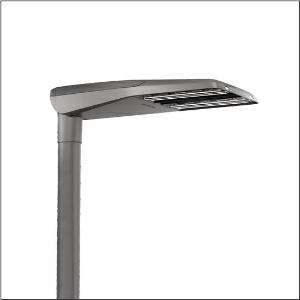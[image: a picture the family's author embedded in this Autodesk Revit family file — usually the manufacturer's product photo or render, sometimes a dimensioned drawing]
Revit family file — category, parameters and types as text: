
# Revit family: streetlight_sl_11_iq_midi___pc-r_5xc3f11f08me_40c1
name_source: partatom
category: Lighting Fixtures
units: mm (PartAtom-declared; Revit-internal decimal feet)

## family parameters
Cut with Voids When Loaded = No
Host = Face
Light Source = No
Part Type = Normal
Room Calculation Point = No
Round Connector Dimension = Use Diameter
Shared = No

## types (1)
- --- (1 x LED, 9590 lm, 124.5 W, 1800K)
    Apparent Load = 125 VA
    CIE Flux Codes = 37 73 96 100 100
    Color Rendering = 70
    Color Temperature = 1800K
    Default Elevation = 1800 mm  [stored 5.90551 ft]
    Description = Streetlight SL 11 iQ midi, mast luminaire, primary light control with 3 zone facetted reflector, of plastic, silver coated, highly specular, primary optical cover: cover, of PMMA, transparent, light distribution: PC-R, light emission: direct distribution, primary light characteristic: asymmetric, right, installation type: post-top, side-entry, LED, High Power LED, rated luminous flux: 9.590lm, luminous efficacy: 77lm/W, light colour: 718, colour temperature: 1800K, control: Street-Remote, Auto-Match, Temp-Guard, Lumen-Switch, Night-Set, Smart-Wire, Light-Fading, Desk-Remote (wireless, voltage-free reading and setting of iQ features in the workshop via application-optimized NFC function/RFID function), optimised constant luminous flux control (CLO 2.0), with cable H07RN-F 5x 1.5mm², mains connection: 230..240V, AC, 50/60Hz, connection cable pre-assembled, cable length: 12,5m, start of lifetime: 125W, end of service life: 132W, reduction: 55W, luminaire housing, of diecast aluminium, powder-coated, Siteco® metallic grey (DB 702S), please order mast flange separately, inclination adjustable without tools: 0°, 5°, 10°, 15° (post-top) | 0°, -5°, -10°, -15° (side-entry), sealing non-destructively replaceable, multi-level sealing system, length: 780mm, width: 376mm, height: 118mm, mast flange for spigot size: 42mm (side-entry): 5XC10008XM4, 60/48mm (side-entry/post-top): 5XC10108XM2, 76/60mm (side-entry/post-top): 5XC10108XM1, equipment: Power, protection rating (complete): IP66, insulation class (complete): insulation class II (safety insulation), certification: CE, ENEC, VDE, impact resistance: IK09, permissible operating ambient temperature for outdoor applications: -25..+50°C, standard-compliant lighting for roads and squares, Environmental Product Declaration (EPD) tested and certified by an independent institute, packaging unit: 1 piece

Light Distribution: PC-R
    Height = 118 mm
    Lamp = 1 x LED
    Lamp Light Flux = 9590 lm
    Lamp Power = 124.5 W
    Lamp count = 1
    Length = 780 mm
    Luminous efficacy = 77 lm/W
    Manufacturer = Siteco
    ModVariant = No
    Model = 5XC3F11F08ME
    Number of Poles = 1
    OnlyDefault = Yes
    Power Factor = 1
    Product Name = Streetlight SL 11 iQ midi | PC-R
    Product group = mast luminaire | pylon top
    ProductGroupID = 6100
    Protection Class = Protection class II
    Protection Degree = IP 66
    RLX_Detail_Level = 1
    RLX_Emergency_Light_Flux = 0 lm
    RLX_Emergency_Type = 0
    RLX_Emergency_Type_DB = No
    RlxData = <blob elided: 74545 chars, md5=f4a8ba47>
    Socket = socket
    Standby Power = 0 W
    System Light Flux = 9590 lm
    System Power = 125 W
    Type Comments = factory setting: luminous flux: 100 % | dim-lin: 254 | 554 mA
    Type Image = l_1005960.jpg
    URL = http://relux.com
    VarID = @adj_009967
    Voltage = 0 V
    Weight = 0.00 kg
    Width = 376 mm

note: [stored X ft] marks values corroborated as IEEE doubles in the binary element streams (Revit-internal decimal feet)

## geometry (parser evidence)
native form markers: Blend x4, Sweep x12
no freeform markers — native parametric forms only
